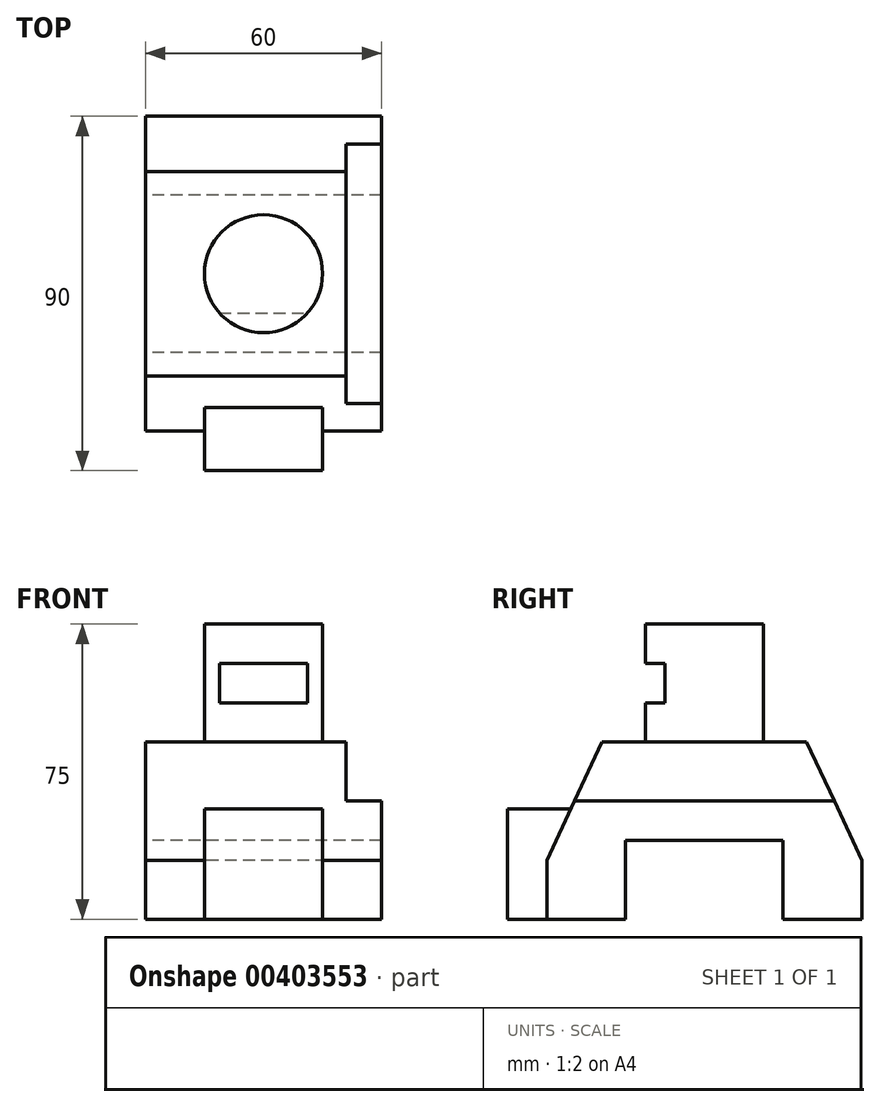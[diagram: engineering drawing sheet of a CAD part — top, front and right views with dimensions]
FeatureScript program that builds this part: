
annotation { "Feature Type Name" : "Feature", "Feature Type Description" : "" }
export const myFeature = defineFeature(function(context is Context, id is Id, definition is map)
    precondition{}
    {
        {
            var Q0;
            Q0=qCreatedBy(makeId("Right.planeOp"),FACE);
            var sketch = newSketch(context, id + "F0", { "sketchPlane" : qUnion([Q0])});
            skLineSegment(sketch, "E0", {"start": v(0, 0) * mm, "end": v(20, 0) * mm});
            skLineSegment(sketch, "E1", {"start": v(20, 0) * mm, "end": v(20, -20) * mm});
            skLineSegment(sketch, "E2", {"start": v(20, -20) * mm, "end": v(40, -20) * mm});
            skLineSegment(sketch, "E3", {"start": v(40, -20) * mm, "end": v(40, -5) * mm});
            skLineSegment(sketch, "E4", {"start": v(40, -5) * mm, "end": v(26, 25) * mm});
            skLineSegment(sketch, "E5", {"start": v(26, 25) * mm, "end": v(0, 25) * mm});
            skLineSegment(sketch, "E6", {"start": v(0, 25) * mm, "end": v(0, 0) * mm, "construction": true});
            skLineSegment(sketch, "E7.MirrorCS", {"start": v(-26, 25) * mm, "end": v(0, 25) * mm});
            skLineSegment(sketch, "E8.MirrorCS", {"start": v(-40, -5) * mm, "end": v(-26, 25) * mm});
            skLineSegment(sketch, "E9.MirrorCS", {"start": v(-40, -20) * mm, "end": v(-40, -5) * mm});
            skLineSegment(sketch, "E10.MirrorCS", {"start": v(-20, -20) * mm, "end": v(-40, -20) * mm});
            skLineSegment(sketch, "E11.MirrorCS", {"start": v(-20, 0) * mm, "end": v(-20, -20) * mm});
            skLineSegment(sketch, "E12.MirrorCS", {"start": v(0, 0) * mm, "end": v(-20, 0) * mm});
            skSolve(sketch);
        }
        {
            var Q0;
            Q0 = qSketchRegion(id + "F0", true);
            extrude(context, id + "F1", {"entities" : qUnion([Q0]), "endBound" : BoundingType.SYMMETRIC, "depth" : 60 * mm});
        }
        {
            var Q0;
            Q0=makeQuery(id+"F1.opExtrude","SWEPT_FACE",FACE,{"disambiguationData":[OSD([sQuery(id+"F0.wireOp",EDGE,"E5"),sQuery(id+"F0.wireOp",EDGE,"E7.MirrorCS")])]});
            var sketch = newSketch(context, id + "F2", { "sketchPlane" : qUnion([Q0])});
            skCircle(sketch, "E13", {"center": v(0, 0) * mm, "radius": 15 * mm});
            skSolve(sketch);
        }
        {
            var Q0;
            Q0 = qSketchRegion(id + "F2", true);
            extrude(context, id + "F3", {"entities" : qUnion([Q0]), "operationType" : NewBodyOperationType.ADD, "depth" : 30 * mm});
        }
        {
            var Q0;
            Q0=makeQuery(id+"F1.opExtrude","SWEPT_FACE",FACE,{"disambiguationData":[OSD([sQuery(id+"F0.wireOp",EDGE,"E9.MirrorCS")])]});
            var sketch = newSketch(context, id + "F4", { "sketchPlane" : qUnion([Q0])});
            skLineSegment(sketch, "E14.bottom", {"start": v(-15, -20) * mm, "end": v(15, -20) * mm});
            skLineSegment(sketch, "E14.top", {"start": v(-15, 8) * mm, "end": v(15, 8) * mm});
            skLineSegment(sketch, "E14.left", {"start": v(-15, -20) * mm, "end": v(-15, 8) * mm});
            skLineSegment(sketch, "E14.right", {"start": v(15, -20) * mm, "end": v(15, 8) * mm});
            skSolve(sketch);
        }
        {
            var Q0;
            Q0 = qSketchRegion(id + "F4", true);
            var Q1;
            Q1=makeQuery(id+"F1.opExtrude","SWEPT_FACE",FACE,{"disambiguationData":[OSD([sQuery(id+"F0.wireOp",EDGE,"E9.MirrorCS")])]});
            extrude(context, id + "F5", {"entities" : qUnion([Q0]), "operationType" : NewBodyOperationType.ADD, "depth" : 10 * mm});
        }
        {
            var Q0;
            Q0 = qSketchRegion(id + "F4", true);
            var Q1;
            Q1=makeQuery(id+"F1.opExtrude","SWEPT_FACE",FACE,{"disambiguationData":[OSD([sQuery(id+"F0.wireOp",EDGE,"E8.MirrorCS")])]});
            extrude(context, id + "F6", {"entities" : qUnion([Q0]), "operationType" : NewBodyOperationType.ADD, "endBound" : BoundingType.UP_TO_SURFACE, "oppositeDirection" : true, "endBoundEntityFace" : qUnion([Q1]), "depth" : 25 * mm});
        }
        {
            var Q0;
            Q0=makeQuery(id+"F1.opExtrude","SWEPT_FACE",FACE,{"disambiguationData":[OSD([sQuery(id+"F0.wireOp",EDGE,"E5"),sQuery(id+"F0.wireOp",EDGE,"E7.MirrorCS")])]});
            var sketch = newSketch(context, id + "F7", { "sketchPlane" : qUnion([Q0])});
            skLineSegment(sketch, "E15.bottom", {"start": v(21, -40) * mm, "end": v(30, -40) * mm});
            skLineSegment(sketch, "E15.top", {"start": v(21, 40) * mm, "end": v(30, 40) * mm});
            skLineSegment(sketch, "E15.left", {"start": v(21, -40) * mm, "end": v(21, 40) * mm});
            skLineSegment(sketch, "E15.right", {"start": v(30, -40) * mm, "end": v(30, 40) * mm});
            skSolve(sketch);
        }
        {
            var Q0;
            Q0 = qSketchRegion(id + "F7", true);
            extrude(context, id + "F8", {"entities" : qUnion([Q0]), "operationType" : NewBodyOperationType.REMOVE, "oppositeDirection" : true, "depth" : 15 * mm});
        }
        {
            var Q0;
            Q0=makeQuery(id+"F5.opExtrude","CAP_FACE",FACE,{"disambiguationData":[OSD([sQuery(id+"F4.wireOp",EDGE,"E14.bottom"),sQuery(id+"F4.wireOp",EDGE,"E14.top"),sQuery(id+"F4.wireOp",EDGE,"E14.left"),sQuery(id+"F4.wireOp",EDGE,"E14.right")])],"isStart":false});
            var sketch = newSketch(context, id + "F9", { "sketchPlane" : qUnion([Q0])});
            skLineSegment(sketch, "E16.bottom", {"start": v(-15, 45) * mm, "end": v(15, 45) * mm});
            skLineSegment(sketch, "E16.top", {"start": v(-15, 35) * mm, "end": v(15, 35) * mm});
            skLineSegment(sketch, "E16.left", {"start": v(-15, 45) * mm, "end": v(-15, 35) * mm});
            skLineSegment(sketch, "E16.right", {"start": v(15, 45) * mm, "end": v(15, 35) * mm});
            skSolve(sketch);
        }
        {
            var Q0;
            Q0 = qSketchRegion(id + "F9", true);
            extrude(context, id + "F10", {"entities" : qUnion([Q0]), "operationType" : NewBodyOperationType.REMOVE, "oppositeDirection" : true, "depth" : 40 * mm});
        }
    });
